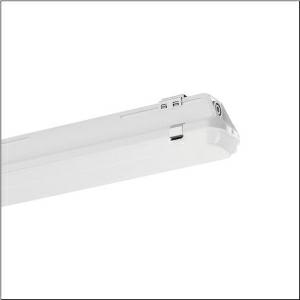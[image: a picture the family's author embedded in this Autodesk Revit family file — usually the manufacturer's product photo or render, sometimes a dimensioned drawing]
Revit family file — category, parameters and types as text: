
# Revit family: monsun_r__21_51fb107p430j005_42d6
name_source: partatom
category: Lighting Fixtures
units: mm (PartAtom-declared; Revit-internal decimal feet)

## family parameters
Cut with Voids When Loaded = No
Host = Face
Light Source = No
Part Type = Normal
Room Calculation Point = No
Round Connector Dimension = Use Diameter
Shared = No

## types (1)
- Monsun® 21 (1 x LED, 3710 lm, 22.2 W, 4000K)
    Apparent Load = 22 VA
    CIE Flux Codes = 47 77 93 94 100
    Color Rendering = 80
    Color Temperature = 4000K
    Default Elevation = 1800 mm
    Description = Monsun® 21, damp-proof luminaire, chain hanger, primary optical cover: enclosure, of PMMA, light emission: direct distribution, primary light characteristic: symmetric, installation type: suspended mounting, surface-mounted, horizontal mounting, vertical mounting, LED, rated luminous flux: 3.710lm, luminous efficacy: 167lm/W, light colour: 840, colour temperature: 4000K, control gear: ECG, with terminal, 3-pole, max. 2.5mm², through-wiring: 5x 2.5mm², mains connection: 220..240V, AC, 50/60Hz, rated input power: 22W, housing, of glass-fibre reinforced polyester, uncoated, bright grey, length: 1.590mm, width: 90mm, height: 88mm, clip for enclosure, of stainless steel (V2A), ceiling mounting element, of stainless steel (V2A), chain hanger, of stainless steel (V2A), protection rating (complete): IP66, insulation class (complete): insulation class I (protective earthing), certification: CE, ENEC, VDE, UKCA, protection symbol: D, impact resistance: IK04, permissible operating ambient temperature: -25..+35°C, standard: EN 50419, EN 60598-2-1, corresponds to IFS (International Featured Standards) requirements for safety and quality in the food industry, for indoor or canopied outdoor use, no direct snow, no direct sun, no direct rain, packaging unit: 1 piece
    Height = 89 mm
    Lamp = 1 x LED
    Lamp Light Flux = 3710 lm
    Lamp Power = 22.2 W
    Lamp count = 1
    Length = 1590 mm
    Luminous efficacy = 167 lm/W
    Manufacturer = Siteco
    ModVariant = No
    Model = 51FB107P430J005
    Mounting Place = Ceiling
    Mounting Type = Pendant
    Number of Poles = 1
    OnlyDefault = Yes
    Power Factor = 1
    Product Name = Monsun® 21
    Product group = damp-proof luminaire | ceiling pendant
    ProductGroupID = 908
    Protection Class = Protection class I
    Protection Degree = IP 66
    RLX_Detail_Level = 1
    RlxData = <blob elided: 88397 chars, md5=c322f439>
    Socket = socket
    Standby Power = 0 W
    System Light Flux = 3710 lm
    System Power = 22 W
    Type Comments = Product without accessories
    Type Image = l_1006717.jpg
    URL = http://relux.com
    VarID = ---
    Voltage = 0 V
    Weight = 0.00 kg
    Width = 90 mm

## geometry (parser evidence)
native form markers: Blend x4, Sweep x13
no freeform markers — native parametric forms only
